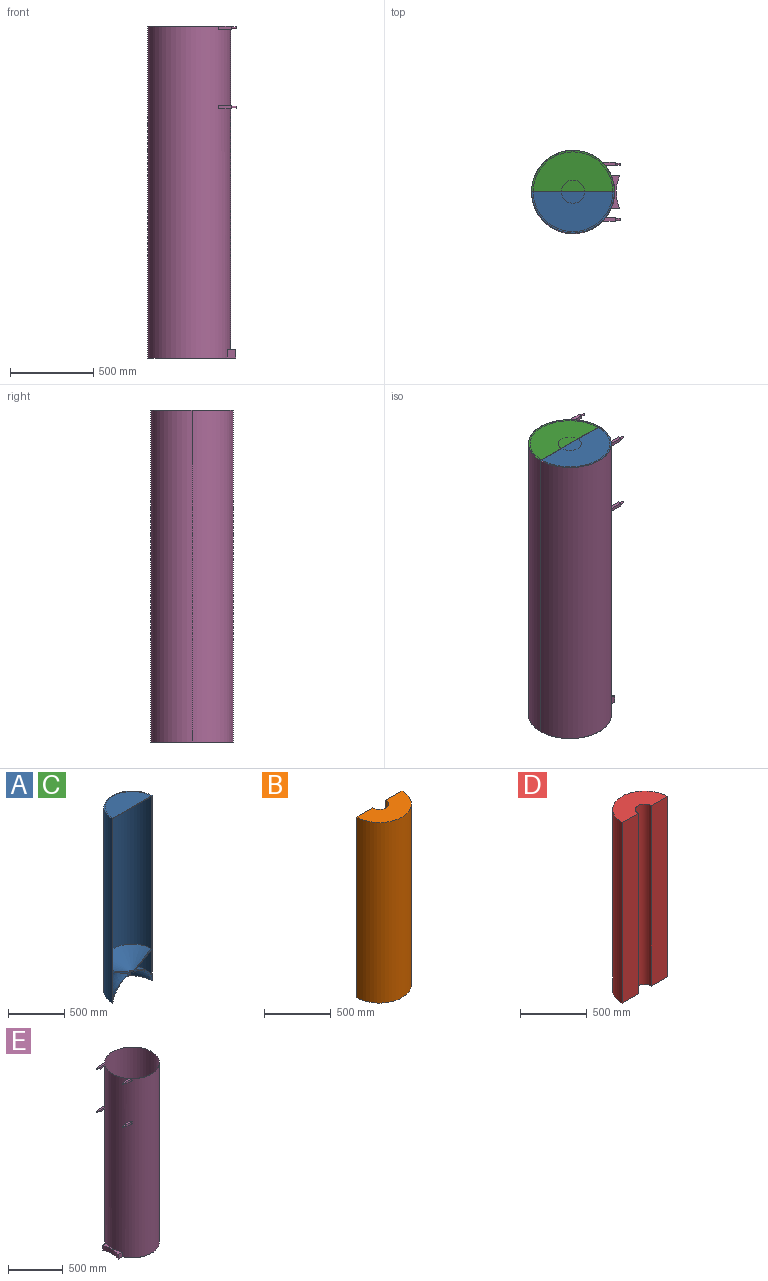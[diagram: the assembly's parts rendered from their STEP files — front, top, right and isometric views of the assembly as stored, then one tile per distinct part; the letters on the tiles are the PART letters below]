
ASSEMBLY  parts=5 mates=4
PART A: 13 faces, bbox 499x249.5x2000 mm
  f0: plane 2000x499mm, normal (0,-1,0), area 54441.9mm2, adj f1,f2,f3,f4,f5,f6,f7,f8
  f1: plane 499x249.5mm, normal (0,0,-1), area 7304.6mm2, adj f0,f4,f8
  f2: plane 499x249.5mm, normal (0,0,1), area 97782.5mm2, adj f0,f8
  f3: cylinder r=20mm len=40mm, axis (0,0,1), area 1256.6mm2, adj f0,f4,f5
  f4: sphere r=244mm, area 152680.3mm2, adj f0,f1,f3
  f5: cone r=20mm half-angle=60.4deg, axis (0,0,1), area 103339.9mm2, adj f0,f3,f6
  f6: cylinder r=240mm len=1654.82mm, axis (0,0,-1), area 1247705.7mm2, adj f0,f5,f7
  f7: plane 480x240mm, normal (0,0,-1), area 90477.9mm2, adj f0,f6
  f8: cylinder r=249.5mm len=2000mm, axis (0,0,1), area 1567654.7mm2, adj f0,f1,f2
  f9: cone r=52.51mm half-angle=59.8deg, axis (0,0,1), area 99633.5mm2, adj f0,f10,f12
  f10: cylinder r=52.51mm len=105.01mm, axis (0,0,1), area 1951.3mm2, adj f0,f9,f11
  f11: revolved ~480x240mm, area 130208.8mm2, adj f0,f10,f12
  f12: cylinder r=240mm len=480mm, axis (0,0,1), area 211115mm2, adj f0,f9,f11
PART B: 6 faces, bbox 480x240x1655 mm
  f0: plane 1655x170mm, normal (0,1,0), area 281350mm2, adj f2,f3,f4,f5
  f1: plane 1655x170mm, normal (0,1,0), area 281350mm2, adj f2,f3,f4,f5
  f2: cylinder r=240mm len=1655mm, axis (0,0,1), area 1247840.6mm2, adj f0,f1,f3,f4
  f3: plane 480x240mm, normal (0,0,-1), area 82781mm2, adj f0,f1,f2,f5
  f4: plane 480x240mm, normal (0,0,1), area 82781mm2, adj f0,f1,f2,f5
  f5: cylinder r=70mm len=1655mm, axis (0,0,1), area 363953.5mm2, adj f0,f1,f3,f4
PART C: same geometry as A
PART D: 6 faces, bbox 480x240x1655 mm
  f0: plane 1655x170mm, normal (0,-1,0), area 281350mm2, adj f2,f3,f4,f5
  f1: plane 1655x170mm, normal (0,-1,0), area 281350mm2, adj f2,f3,f4,f5
  f2: cylinder r=240mm len=1655mm, axis (0,0,1), area 1247840.6mm2, adj f0,f1,f3,f4
  f3: plane 480x240mm, normal (0,0,-1), area 82781mm2, adj f0,f1,f2,f5
  f4: plane 480x240mm, normal (0,0,1), area 82781mm2, adj f0,f1,f2,f5
  f5: cylinder r=70mm len=1655mm, axis (0,0,1), area 363953.5mm2, adj f0,f1,f3,f4
PART E: 34 faces, bbox 535x500x2000 mm
  f0: plane 60.27x20mm, normal (0,-1,0), area 1205.3mm2, adj f5,f8,f11,f23
  f1: plane 60.27x20mm, normal (0,1,0), area 1205.3mm2, adj f9,f10,f11,f22
  f2: plane 505x500mm, normal (0,0,1), area 3541.5mm2, adj f3,f11,f13,f14,f15,f21,f24,f25
  f3: plane 78.22x20mm, normal (0,-1,0), area 1564.5mm2, adj f2,f6,f11,f25
  f4: plane 78.22x20mm, normal (0,-1,0), area 1564.5mm2, adj f9,f10,f11,f22
  f5: plane 78.22x20mm, normal (0,0,1), area 1378.4mm2, adj f0,f11,f12,f23
  f6: plane 78.22x20mm, normal (0,0,-1), area 1378.4mm2, adj f3,f11,f14,f25
  f7: plane 78.22x20mm, normal (0,0,-1), area 1378.4mm2, adj f11,f13,f15,f24
  f8: plane 78.22x20mm, normal (0,0,-1), area 1378.4mm2, adj f0,f11,f12,f23
  f9: plane 78.22x20mm, normal (0,0,-1), area 1378.4mm2, adj f1,f4,f11,f22
  f10: plane 78.22x20mm, normal (0,0,1), area 1378.4mm2, adj f1,f4,f11,f22
  f11: cylinder r=250mm len=2000mm, axis (0,0,-1), area 3129153.4mm2, adj f0,f1,f2,f3,f4,f5,f6,f7
  f12: plane 78.22x20mm, normal (0,1,0), area 1564.5mm2, adj f5,f8,f11,f23
  f13: plane 78.22x20mm, normal (0,1,0), area 1564.5mm2, adj f2,f7,f11,f24
  f14: plane 60.27x20mm, normal (0,1,0), area 1205.3mm2, adj f2,f6,f11,f25
  f15: plane 60.27x20mm, normal (0,-1,0), area 1205.3mm2, adj f2,f7,f11,f24
  f16: plane 530.87x500mm, normal (0,0,-1), area 5519.3mm2, adj f11,f17,f18,f19,f21
  f17: plane 51.74x50mm, normal (0,1,0), area 2587.1mm2, adj f11,f16,f18,f20
  f18: cylinder r=250mm len=200mm, axis (0,0,-1), area 10287.9mm2, adj f16,f17,f19,f20
  f19: plane 51.74x50mm, normal (0,-1,0), area 2587.1mm2, adj f11,f16,f18,f20
  f20: plane 200x51.74mm, normal (0,0,1), area 4734.6mm2, adj f11,f17,f18,f19
  f21: cylinder r=249.5mm len=2000mm, axis (0,0,1), area 3135309.5mm2, adj f2,f16
  f22: plane 20x20mm, normal (-1,0,0), area 286.9mm2, adj f1,f4,f9,f10,f30
  f23: plane 20x20mm, normal (-1,0,0), area 286.9mm2, adj f0,f5,f8,f12,f32
  f24: plane 20x20mm, normal (-1,0,0), area 286.9mm2, adj f2,f7,f13,f15,f26
  f25: plane 20x20mm, normal (-1,0,0), area 286.9mm2, adj f2,f3,f6,f14,f28
  f26: cylinder r=6mm len=30mm, axis (1,0,0), area 1131mm2, adj f24,f27
  f27: plane 12x12mm, normal (-1,0,0), area 113.1mm2, adj f26
  f28: cylinder r=6mm len=30mm, axis (1,0,0), area 1131mm2, adj f25,f29
  f29: plane 12x12mm, normal (-1,0,0), area 113.1mm2, adj f28
  f30: cylinder r=6mm len=30mm, axis (1,0,0), area 1131mm2, adj f22,f31
  f31: plane 12x12mm, normal (-1,0,0), area 113.1mm2, adj f30
  f32: cylinder r=6mm len=30mm, axis (1,0,0), area 1131mm2, adj f23,f33
  f33: plane 12x12mm, normal (-1,0,0), area 113.1mm2, adj f32
PLACE A rot(axis=(0,0,1),180deg) t=(-225.18,184.6,-340.96)mm
PLACE B t=(-225.18,184.6,-341.96)mm
PLACE C t=(-225.18,184.6,-340.96)mm fixed
PLACE D t=(-225.18,184.6,-341.96)mm
PLACE E rot(axis=(0,0,1),180deg) t=(-225.18,184.6,-340.96)mm
MATE fastened E.f21 <-> C.f5  axis (0,0,1) through (-225.18,184.6,-340.96)mm
MATE fastened D.f5 <-> B.f2  axis (0,0,1) through (-225.18,184.6,1657.04)mm
MATE fastened D.f5 <-> C.f6  axis (0,0,1) through (-225.18,184.6,1657.04)mm
MATE fastened C.f5 <-> A.f5  axis (0,0,1) through (-225.18,184.6,1659.04)mm
